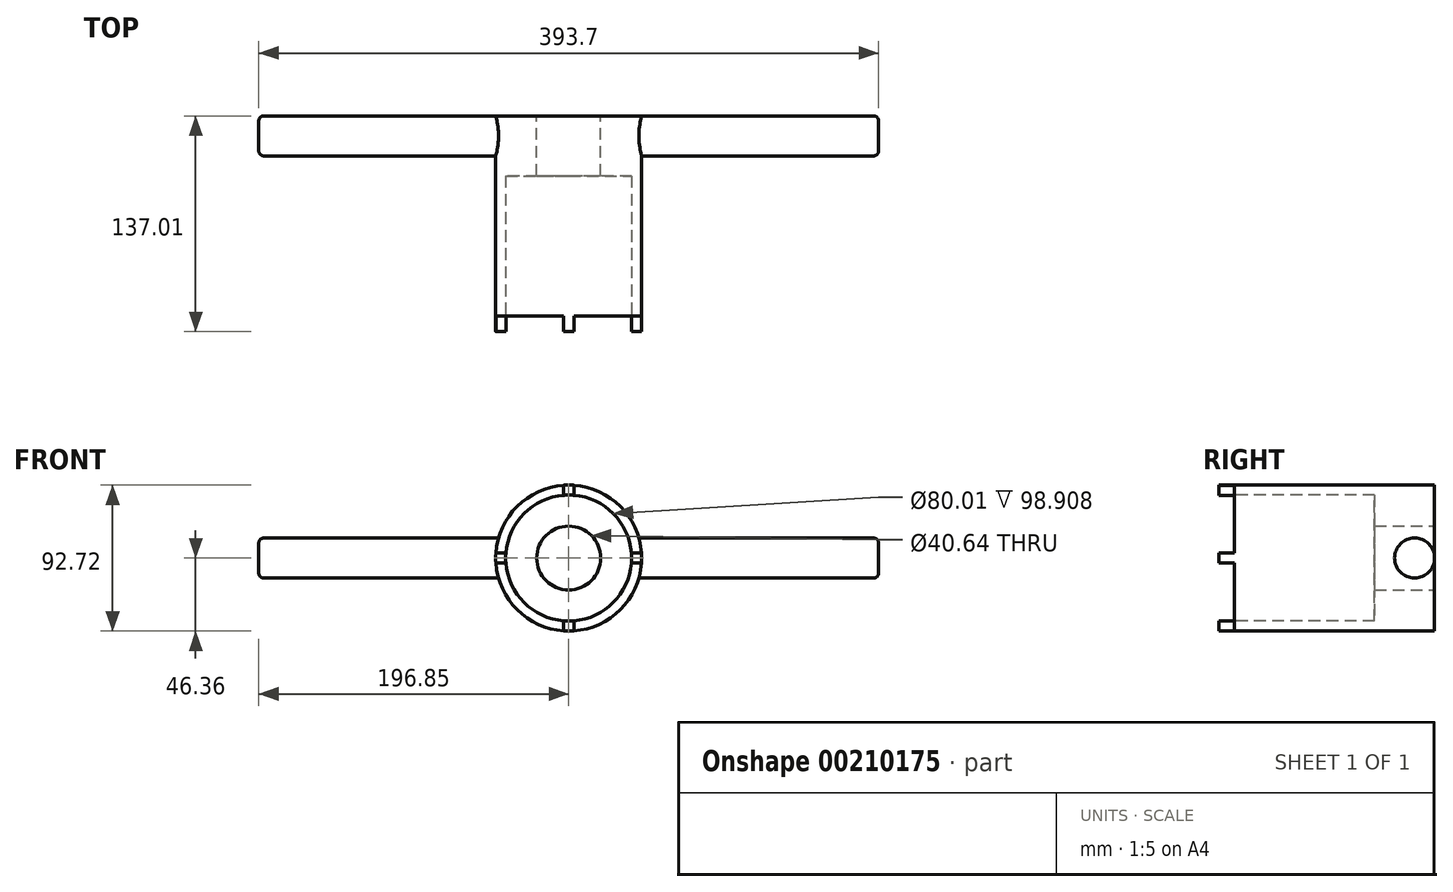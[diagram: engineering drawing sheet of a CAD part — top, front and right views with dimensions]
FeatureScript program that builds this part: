
annotation { "Feature Type Name" : "Feature", "Feature Type Description" : "" }
export const myFeature = defineFeature(function(context is Context, id is Id, definition is map)
    precondition{}
    {
        {
            var Q0;
            Q0=qCreatedBy(makeId("Front.planeOp"),FACE);
            var sketch = newSketch(context, id + "F0", { "sketchPlane" : qUnion([Q0])});
            skCircle(sketch, "E0", {"center": v(0, 0) * mm, "radius": 40 * mm});
            skCircle(sketch, "E1", {"center": v(0, 0) * mm, "radius": 46.35 * mm});
            skSolve(sketch);
        }
        {
            var Q0;
            Q0=makeQuery(id+"F0.imprint","IMPRINT",FACE,{"disambiguationData":[TD([[makeQuery(id+"F0.imprint","IMPRINT",EDGE,{"derivedFrom":sQuery(id+"F0.wireOp",EDGE,"E0")}),-1.0]])]});
            extrude(context, id + "F1", {"entities" : qUnion([Q0]), "oppositeDirection" : true, "depth" : 127 * mm, "offsetDistance" : 25.4 * mm});
        }
        {
            var Q0;
            Q0=makeQuery(id+"F1.opExtrude","CAP_FACE",FACE,{"disambiguationData":[OSD([sQuery(id+"F0.wireOp",EDGE,"E0"),sQuery(id+"F0.wireOp",EDGE,"E1")])],"isStart":true});
            var sketch = newSketch(context, id + "F2", { "sketchPlane" : qUnion([Q0])});
            skLineSegment(sketch, "E2.bottom", {"start": v(0, 48.23) * mm, "end": v(3.25, 48.23) * mm});
            skLineSegment(sketch, "E2.top", {"start": v(0, -47.48) * mm, "end": v(3.25, -47.48) * mm});
            skLineSegment(sketch, "E2.left", {"start": v(0, 48.23) * mm, "end": v(0, -47.48) * mm});
            skLineSegment(sketch, "E2.right", {"start": v(3.25, 48.23) * mm, "end": v(3.25, -47.48) * mm});
            skLineSegment(sketch, "E3.MirrorCS", {"start": v(0, 48.23) * mm, "end": v(-3.25, 48.23) * mm});
            skLineSegment(sketch, "E4.MirrorCS", {"start": v(-3.25, 48.23) * mm, "end": v(-3.25, -47.48) * mm});
            skLineSegment(sketch, "E5.MirrorCS", {"start": v(0, -47.48) * mm, "end": v(-3.25, -47.48) * mm});
            skSolve(sketch);
        }
        {
            var Q0;
            {var subQ0=sQuery(id+"F2.wireOp",EDGE,"E4.MirrorCS");var subQ1=makeQuery(id+"F1.opExtrude","CAP_EDGE",EDGE,{"disambiguationData":[OSD([sQuery(id+"F0.wireOp",EDGE,"E1")])],"isStart":true});var subQ2=makeQuery(id+"F2.imprint","INTERSECT",VERTEX,{"disambiguationData":[OD(0.0)],"derivedFrom":[subQ1,subQ0]});Q0=makeQuery(id+"F2.imprint","IMPRINT",FACE,{"disambiguationData":[TD([[makeQuery(id+"F2.imprint","IMPRINT",EDGE,{"disambiguationData":[TD([[subQ2,-1.0]])],"derivedFrom":subQ0}),-1.0]])]});}
            var sketch = newSketch(context, id + "F3", { "sketchPlane" : qUnion([Q0])});
            skLineSegment(sketch, "E6.bottom", {"start": v(0, 0) * mm, "end": v(50.37, 0) * mm});
            skLineSegment(sketch, "E6.top", {"start": v(0, 3.25) * mm, "end": v(50.37, 3.25) * mm});
            skLineSegment(sketch, "E6.left", {"start": v(0, 0) * mm, "end": v(0, 3.25) * mm});
            skLineSegment(sketch, "E6.right", {"start": v(50.37, 0) * mm, "end": v(50.37, 3.25) * mm});
            skLineSegment(sketch, "E7.MirrorCS", {"start": v(0, -3.25) * mm, "end": v(50.37, -3.25) * mm});
            skLineSegment(sketch, "E8.MirrorCS", {"start": v(50.37, 0) * mm, "end": v(50.37, -3.25) * mm});
            skLineSegment(sketch, "E9.MirrorCS", {"start": v(0, -3.25) * mm, "end": v(-50.37, -3.25) * mm});
            skLineSegment(sketch, "E10.MirrorCS", {"start": v(0, 3.25) * mm, "end": v(-50.37, 3.25) * mm});
            skLineSegment(sketch, "E11.MirrorCS", {"start": v(-50.37, 0) * mm, "end": v(-50.37, -3.25) * mm});
            skLineSegment(sketch, "E12.MirrorCS", {"start": v(-50.37, 0) * mm, "end": v(-50.37, 3.25) * mm});
            skSolve(sketch);
        }
        {
            var Q0;
            {var subQ0=sQuery(id+"F2.wireOp",EDGE,"E2.left");var subQ1=makeQuery(id+"F1.opExtrude","CAP_EDGE",EDGE,{"disambiguationData":[OSD([sQuery(id+"F0.wireOp",EDGE,"E1")])],"isStart":true});var subQ2=makeQuery(id+"F2.imprint","INTERSECT",VERTEX,{"disambiguationData":[OD(0.0)],"derivedFrom":[subQ1,subQ0]});Q0=makeQuery(id+"F2.imprint","IMPRINT",FACE,{"disambiguationData":[TD([[makeQuery(id+"F2.imprint","IMPRINT",EDGE,{"disambiguationData":[TD([[subQ2,-1.0]])],"derivedFrom":subQ0}),-1.0]])]});}
            var Q1;
            {var subQ0=sQuery(id+"F2.wireOp",EDGE,"E2.left");var subQ1=makeQuery(id+"F1.opExtrude","CAP_EDGE",EDGE,{"disambiguationData":[OSD([sQuery(id+"F0.wireOp",EDGE,"E1")])],"isStart":true});var subQ2=makeQuery(id+"F2.imprint","INTERSECT",VERTEX,{"disambiguationData":[OD(0.0)],"derivedFrom":[subQ1,subQ0]});Q1=makeQuery(id+"F2.imprint","IMPRINT",FACE,{"disambiguationData":[TD([[makeQuery(id+"F2.imprint","IMPRINT",EDGE,{"disambiguationData":[TD([[subQ2,-1.0]])],"derivedFrom":subQ0}),1.0]])]});}
            var Q2;
            {var subQ0=sQuery(id+"F2.wireOp",EDGE,"E2.left");var subQ1=makeQuery(id+"F1.opExtrude","CAP_EDGE",EDGE,{"disambiguationData":[OSD([sQuery(id+"F0.wireOp",EDGE,"E0")])],"isStart":true});var subQ2=makeQuery(id+"F2.imprint","INTERSECT",VERTEX,{"disambiguationData":[OD(1.0)],"derivedFrom":[subQ1,subQ0]});Q2=makeQuery(id+"F2.imprint","IMPRINT",FACE,{"disambiguationData":[TD([[makeQuery(id+"F2.imprint","IMPRINT",EDGE,{"disambiguationData":[TD([[subQ2,-1.0]])],"derivedFrom":subQ0}),1.0]])]});}
            var Q3;
            {var subQ0=sQuery(id+"F2.wireOp",EDGE,"E2.left");var subQ1=makeQuery(id+"F1.opExtrude","CAP_EDGE",EDGE,{"disambiguationData":[OSD([sQuery(id+"F0.wireOp",EDGE,"E0")])],"isStart":true});var subQ2=makeQuery(id+"F2.imprint","INTERSECT",VERTEX,{"disambiguationData":[OD(1.0)],"derivedFrom":[subQ1,subQ0]});Q3=makeQuery(id+"F2.imprint","IMPRINT",FACE,{"disambiguationData":[TD([[makeQuery(id+"F2.imprint","IMPRINT",EDGE,{"disambiguationData":[TD([[subQ2,-1.0]])],"derivedFrom":subQ0}),-1.0]])]});}
            var Q4;
            {var subQ0=sQuery(id+"F3.wireOp",EDGE,"E9.MirrorCS");var subQ1=sQuery(id+"F2.wireOp",EDGE,"E4.MirrorCS");var subQ2=makeQuery(id+"F1.opExtrude","CAP_EDGE",EDGE,{"disambiguationData":[OSD([sQuery(id+"F0.wireOp",EDGE,"E0")])],"isStart":true});var subQ3=makeQuery(id+"F2.imprint","IMPRINT",EDGE,{"disambiguationData":[TD([[makeQuery(id+"F2.imprint","INTERSECT",VERTEX,{"disambiguationData":[OD(0.0)],"derivedFrom":[subQ2,subQ1]}),-1.0]])],"derivedFrom":subQ2});var subQ4=makeQuery(id+"F3.imprint","INTERSECT",VERTEX,{"derivedFrom":[subQ3,subQ0]});Q4=makeQuery(id+"F3.imprint","IMPRINT",FACE,{"disambiguationData":[TD([[makeQuery(id+"F3.imprint","IMPRINT",EDGE,{"disambiguationData":[TD([[subQ4,-1.0]])],"derivedFrom":subQ0}),-1.0]])]});}
            extrude(context, id + "F4", {"entities" : qUnion([Q0, Q1, Q2, Q3, Q4]), "operationType" : NewBodyOperationType.ADD, "depth" : 10 * mm});
        }
        {
            var Q0;
            {var subQ0=sQuery(id+"F2.wireOp",EDGE,"E2.right");var subQ1=sQuery(id+"F0.wireOp",EDGE,"E1");var subQ2=makeQuery(id+"F1.opExtrude","CAP_EDGE",EDGE,{"disambiguationData":[OSD([subQ1])],"isStart":true});var subQ4=sQuery(id+"F0.wireOp",EDGE,"E0");var subQ16=makeQuery(id+"F2.imprint","INTERSECT",VERTEX,{"disambiguationData":[OD(0.0)],"derivedFrom":[subQ2,subQ0]});Q0=makeQuery(id+"F4.boolean.opBoolean","SPLIT",FACE,{"disambiguationData":[TD([makeQuery(id+"F4.opExtrude","SWEPT_FACE",FACE,{"disambiguationData":[OSD([subQ0]),TDD([makeQuery(id+"F2.imprint","IMPRINT",EDGE,{"disambiguationData":[TD([[subQ16,-1.0]])],"derivedFrom":subQ0})])]})])],"derivedFrom":makeQuery(id+"F1.opExtrude","CAP_FACE",FACE,{"disambiguationData":[OSD([subQ4,subQ1])],"isStart":true})});}
            var sketch = newSketch(context, id + "F5", { "sketchPlane" : qUnion([Q0])});
            skLineSegment(sketch, "E13.bottom", {"start": v(0, 0) * mm, "end": v(46.56, 0) * mm});
            skLineSegment(sketch, "E13.top", {"start": v(0, 3.25) * mm, "end": v(46.56, 3.25) * mm});
            skLineSegment(sketch, "E13.left", {"start": v(0, 0) * mm, "end": v(0, 3.25) * mm});
            skLineSegment(sketch, "E13.right", {"start": v(46.56, 0) * mm, "end": v(46.56, 3.25) * mm});
            skLineSegment(sketch, "E14.MirrorCS", {"start": v(0, -3.25) * mm, "end": v(46.56, -3.25) * mm});
            skLineSegment(sketch, "E15.MirrorCS", {"start": v(46.56, 0) * mm, "end": v(46.56, -3.25) * mm});
            skSolve(sketch);
        }
        {
            var Q0;
            {var subQ0=sQuery(id+"F5.wireOp",EDGE,"E13.bottom");var subQ1=sQuery(id+"F2.wireOp",EDGE,"E2.right");var subQ2=sQuery(id+"F0.wireOp",EDGE,"E1");var subQ3=makeQuery(id+"F1.opExtrude","CAP_EDGE",EDGE,{"disambiguationData":[OSD([subQ2])],"isStart":true});var subQ13=makeQuery(id+"F2.imprint","INTERSECT",VERTEX,{"disambiguationData":[OD(0.0)],"derivedFrom":[subQ3,subQ1]});var subQ15=makeQuery(id+"F4.opExtrude","SWEPT_FACE",FACE,{"disambiguationData":[OSD([subQ1]),TDD([makeQuery(id+"F2.imprint","IMPRINT",EDGE,{"disambiguationData":[TD([[subQ13,-1.0]])],"derivedFrom":subQ1})])]});var subQ29=makeQuery(id+"F4.boolean.opBoolean","SPLIT",EDGE,{"disambiguationData":[TD([subQ15])],"derivedFrom":subQ3});var subQ30=makeQuery(id+"F5.imprint","INTERSECT",VERTEX,{"derivedFrom":[subQ29,subQ0]});Q0=makeQuery(id+"F5.imprint","IMPRINT",FACE,{"disambiguationData":[TD([[makeQuery(id+"F5.imprint","IMPRINT",EDGE,{"disambiguationData":[TD([[subQ30,1.0]])],"derivedFrom":subQ0}),1.0]])]});}
            var Q1;
            {var subQ0=sQuery(id+"F5.wireOp",EDGE,"E13.bottom");var subQ1=sQuery(id+"F2.wireOp",EDGE,"E2.right");var subQ2=sQuery(id+"F0.wireOp",EDGE,"E1");var subQ3=makeQuery(id+"F1.opExtrude","CAP_EDGE",EDGE,{"disambiguationData":[OSD([subQ2])],"isStart":true});var subQ13=makeQuery(id+"F2.imprint","INTERSECT",VERTEX,{"disambiguationData":[OD(0.0)],"derivedFrom":[subQ3,subQ1]});var subQ15=makeQuery(id+"F4.opExtrude","SWEPT_FACE",FACE,{"disambiguationData":[OSD([subQ1]),TDD([makeQuery(id+"F2.imprint","IMPRINT",EDGE,{"disambiguationData":[TD([[subQ13,-1.0]])],"derivedFrom":subQ1})])]});var subQ29=makeQuery(id+"F4.boolean.opBoolean","SPLIT",EDGE,{"disambiguationData":[TD([subQ15])],"derivedFrom":subQ3});var subQ30=makeQuery(id+"F5.imprint","INTERSECT",VERTEX,{"derivedFrom":[subQ29,subQ0]});Q1=makeQuery(id+"F5.imprint","IMPRINT",FACE,{"disambiguationData":[TD([[makeQuery(id+"F5.imprint","IMPRINT",EDGE,{"disambiguationData":[TD([[subQ30,1.0]])],"derivedFrom":subQ0}),-1.0]])]});}
            extrude(context, id + "F6", {"entities" : qUnion([Q0, Q1]), "operationType" : NewBodyOperationType.ADD, "depth" : 10 * mm});
        }
        {
            var Q0;
            Q0=qCreatedBy(makeId("Right.planeOp"),FACE);
            var sketch = newSketch(context, id + "F7", { "sketchPlane" : qUnion([Q0])});
            skCircle(sketch, "E16", {"center": v(114.3, 0) * mm, "radius": 12.7 * mm});
            skSolve(sketch);
        }
        {
            var Q0;
            Q0=makeQuery(id+"F7.imprint","IMPRINT",FACE,{"disambiguationData":[TD([[makeQuery(id+"F7.imprint","IMPRINT",EDGE,{"derivedFrom":sQuery(id+"F7.wireOp",EDGE,"E16")}),1.0]])]});
            cPlane(context, id + "F8", {"entities" : qUnion([Q0]), "cplaneType" : CPlaneType.OFFSET, "offset" : 40 * mm, "width" : 152.4 * mm, "height" : 152.4 * mm});
        }
        {
            var Q0;
            Q0=qCreatedBy(id+"F8.planeOp",FACE);
            var sketch = newSketch(context, id + "F9", { "sketchPlane" : qUnion([Q0])});
            skCircle(sketch, "E17", {"center": v(114.3, 0) * mm, "radius": 12.7 * mm});
            skSolve(sketch);
        }
        {
            var Q0;
            Q0=qSketchRegion(id+"F9",true);
            extrude(context, id + "F10", {"entities" : qUnion([Q0]), "operationType" : NewBodyOperationType.ADD, "depth" : 156.84 * mm});
        }
        {
            var Q0;
            Q0=makeQuery(id+"F10.opExtrude","CAP_EDGE",EDGE,{"disambiguationData":[OSD([sQuery(id+"F9.wireOp",EDGE,"E17")])],"isStart":false});
            fillet(context, id + "F11", {"entities" : qUnion([Q0]), "radius" : 3.17 * mm, "tangentPropagation" : true, "allowEdgeOverflow" : false});
        }
        {
            var Q0;
            Q0=makeQuery(id+"F1.opExtrude","SWEPT_BODY",BODY,{"disambiguationData":[OSD([sQuery(id+"F0.wireOp",EDGE,"E0"),sQuery(id+"F0.wireOp",EDGE,"E1")])]});
            var Q1;
            Q1=qCreatedBy(makeId("Right.planeOp"),FACE);
            mirror(context, id + "F12", {"operationType" : NewBodyOperationType.ADD, "entities" : qUnion([Q0]), "mirrorPlane" : qUnion([Q1])});
        }
        {
            var Q0;
            Q0=makeQuery(id+"F1.opExtrude","CAP_FACE",FACE,{"disambiguationData":[OSD([sQuery(id+"F0.wireOp",EDGE,"E0"),sQuery(id+"F0.wireOp",EDGE,"E1")])],"isStart":false});
            var sketch = newSketch(context, id + "F13", { "sketchPlane" : qUnion([Q0])});
            skCircle(sketch, "E18", {"center": v(0, 0) * mm, "radius": 20.32 * mm});
            skSolve(sketch);
        }
        {
            var Q0;
            Q0=makeQuery(id+"F13.imprint","IMPRINT",FACE,{"disambiguationData":[TD([[makeQuery(id+"F13.imprint","IMPRINT",EDGE,{"derivedFrom":sQuery(id+"F13.wireOp",EDGE,"E18")}),-1.0]])]});
            extrude(context, id + "F14", {"entities" : qUnion([Q0]), "operationType" : NewBodyOperationType.ADD, "oppositeDirection" : true, "depth" : 38.1 * mm, "offsetDistance" : 25.4 * mm});
        }
    });
